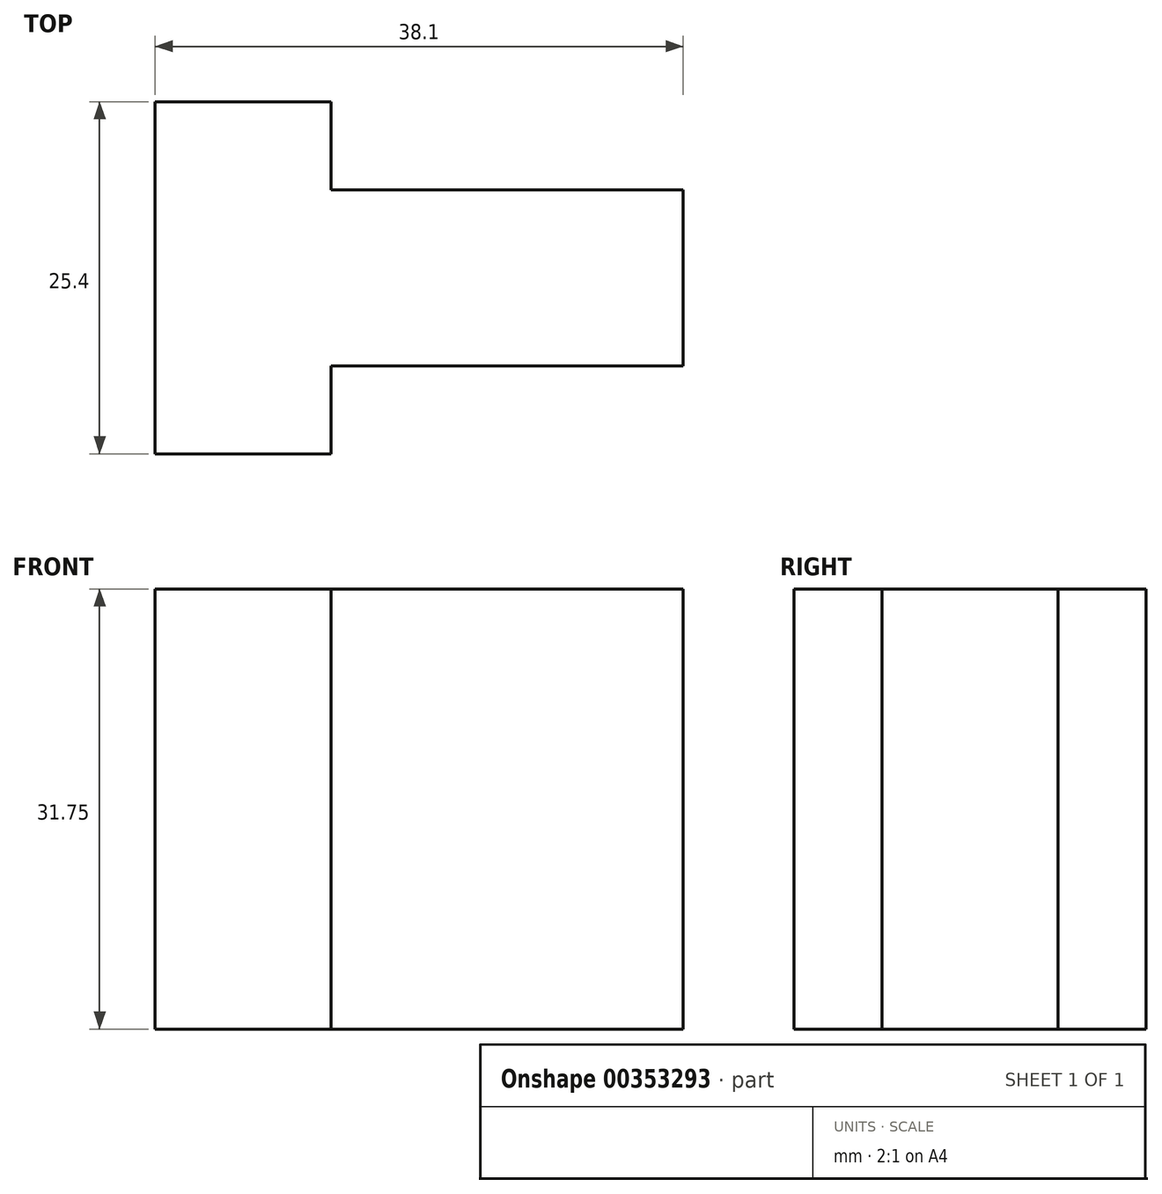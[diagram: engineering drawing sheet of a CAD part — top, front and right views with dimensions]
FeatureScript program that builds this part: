
annotation { "Feature Type Name" : "Feature", "Feature Type Description" : "" }
export const myFeature = defineFeature(function(context is Context, id is Id, definition is map)
    precondition{}
    {
        {
            var Q0;
            Q0=qCreatedBy(makeId("Top.planeOp"),FACE);
            var sketch = newSketch(context, id + "F0", { "sketchPlane" : qUnion([Q0])});
            skLineSegment(sketch, "E0", {"start": v(0, 0) * mm, "end": v(0, 25.4) * mm});
            skLineSegment(sketch, "E1", {"start": v(0, 25.4) * mm, "end": v(12.7, 25.4) * mm});
            skLineSegment(sketch, "E2", {"start": v(12.7, 25.4) * mm, "end": v(12.7, 19.05) * mm});
            skLineSegment(sketch, "E3", {"start": v(12.7, 19.05) * mm, "end": v(38.1, 19.05) * mm});
            skLineSegment(sketch, "E4", {"start": v(38.1, 19.05) * mm, "end": v(38.1, 6.35) * mm});
            skLineSegment(sketch, "E5", {"start": v(38.1, 6.35) * mm, "end": v(12.7, 6.35) * mm});
            skLineSegment(sketch, "E6", {"start": v(12.7, 6.35) * mm, "end": v(12.7, 0) * mm});
            skLineSegment(sketch, "E7", {"start": v(12.7, 0) * mm, "end": v(0, 0) * mm});
            skSolve(sketch);
        }
        {
            var Q0;
            Q0 = qSketchRegion(id + "F0", true);
            extrude(context, id + "F1", {"entities" : qUnion([Q0]), "oppositeDirection" : true, "depth" : 31.75 * mm});
        }
    });
